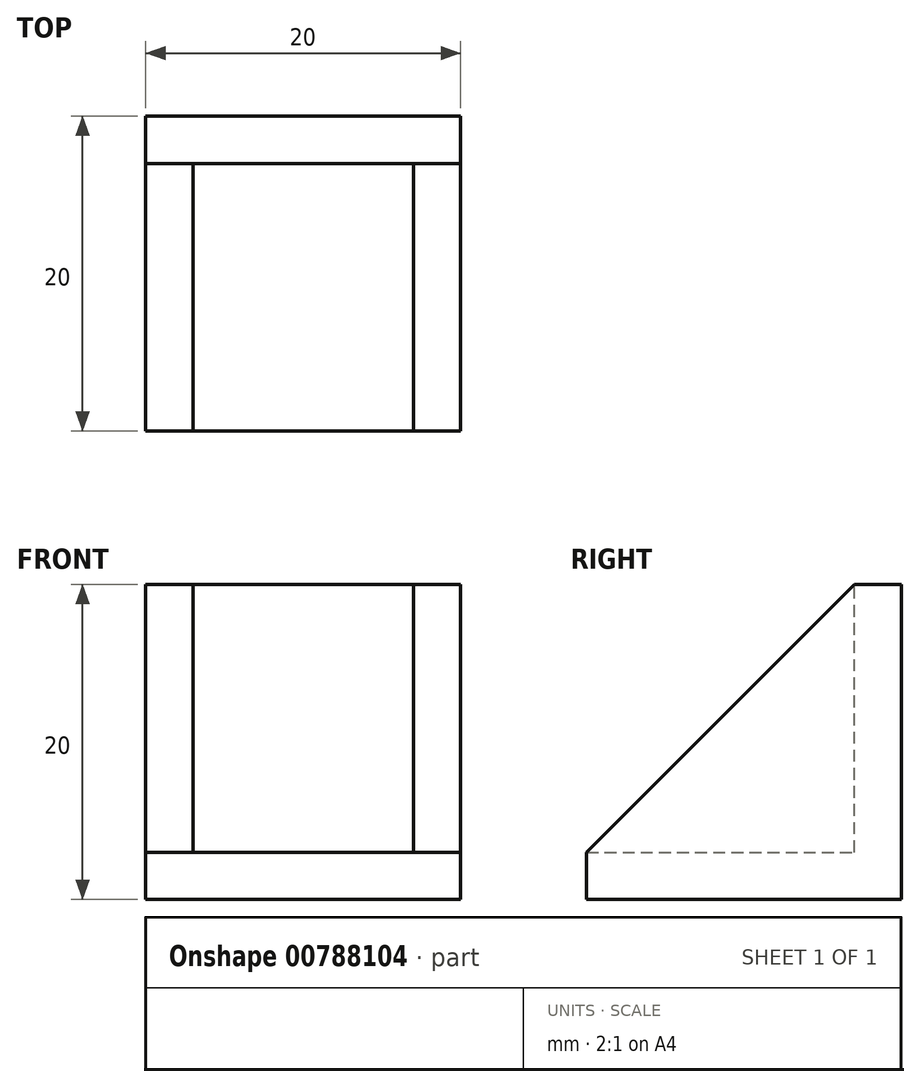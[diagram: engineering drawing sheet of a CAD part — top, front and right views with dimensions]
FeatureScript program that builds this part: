
annotation { "Feature Type Name" : "Feature", "Feature Type Description" : "" }
export const myFeature = defineFeature(function(context is Context, id is Id, definition is map)
    precondition{}
    {
        {
            var Q0;
            Q0=qCreatedBy(makeId("Front.planeOp"),FACE);
            var sketch = newSketch(context, id + "F0", { "sketchPlane" : qUnion([Q0])});
            skLineSegment(sketch, "E0.bottom", {"start": v(0, 0) * mm, "end": v(20, 0) * mm});
            skLineSegment(sketch, "E0.top", {"start": v(0, 20) * mm, "end": v(20, 20) * mm});
            skLineSegment(sketch, "E0.left", {"start": v(0, 0) * mm, "end": v(0, 20) * mm});
            skLineSegment(sketch, "E0.right", {"start": v(20, 0) * mm, "end": v(20, 20) * mm});
            skLineSegment(sketch, "E1", {"start": v(10, 0) * mm, "end": v(10, 8.5) * mm, "construction": true});
            skLineSegment(sketch, "E2", {"start": v(10, 8.5) * mm, "end": v(10, 11.5) * mm, "construction": true});
            skCircle(sketch, "E3", {"center": v(10, 8.5) * mm, "radius": 3 * mm});
            skCircle(sketch, "E4", {"center": v(10, 11.5) * mm, "radius": 3 * mm});
            skLineSegment(sketch, "E5", {"start": v(13, 11.5) * mm, "end": v(13, 8.5) * mm});
            skLineSegment(sketch, "E6", {"start": v(7, 8.5) * mm, "end": v(7, 11.5) * mm});
            skLineSegment(sketch, "E7", {"start": v(20, 0) * mm, "end": v(17, 0) * mm});
            skLineSegment(sketch, "E8", {"start": v(17, 0) * mm, "end": v(17, 20) * mm});
            skLineSegment(sketch, "E9", {"start": v(0, 0) * mm, "end": v(3, 0) * mm});
            skLineSegment(sketch, "E10", {"start": v(3, 0) * mm, "end": v(3, 20) * mm});
            skLineSegment(sketch, "E11", {"start": v(0, 0) * mm, "end": v(0, 3) * mm});
            skLineSegment(sketch, "E12", {"start": v(0, 3) * mm, "end": v(20, 3) * mm});
            skSolve(sketch);
        }
        {
            var Q0;
            {var subQ0=sQuery(id+"F0.wireOp",EDGE,"E0.right");var subQ1=sQuery(id+"F0.wireOp",EDGE,"E0.top");var subQ2=makeQuery(id+"F0.imprint","INTERSECT",VERTEX,{"derivedFrom":[subQ1,subQ0]});Q0=makeQuery(id+"F0.imprint","IMPRINT",FACE,{"disambiguationData":[TD([[makeQuery(id+"F0.imprint","IMPRINT",EDGE,{"disambiguationData":[TD([[subQ2,1.0]])],"derivedFrom":subQ1}),-1.0]])]});}
            var Q1;
            {var subQ0=sQuery(id+"F0.wireOp",EDGE,"E10");var subQ1=sQuery(id+"F0.wireOp",EDGE,"E0.top");var subQ2=makeQuery(id+"F0.imprint","INTERSECT",VERTEX,{"derivedFrom":[subQ1,subQ0]});Q1=makeQuery(id+"F0.imprint","IMPRINT",FACE,{"disambiguationData":[TD([[makeQuery(id+"F0.imprint","IMPRINT",EDGE,{"disambiguationData":[TD([[subQ2,1.0]])],"derivedFrom":subQ1}),-1.0]])]});}
            var Q2;
            {var subQ0=sQuery(id+"F0.wireOp",EDGE,"E10");var subQ1=sQuery(id+"F0.wireOp",EDGE,"E0.bottom");var subQ2=makeQuery(id+"F0.imprint","INTERSECT",VERTEX,{"derivedFrom":[subQ1,subQ0]});Q2=makeQuery(id+"F0.imprint","IMPRINT",FACE,{"disambiguationData":[TD([[makeQuery(id+"F0.imprint","IMPRINT",EDGE,{"disambiguationData":[TD([[subQ2,1.0]])],"derivedFrom":subQ1}),1.0]])]});}
            var Q3;
            {var subQ0=sQuery(id+"F0.wireOp",EDGE,"E10");var subQ1=sQuery(id+"F0.wireOp",EDGE,"E0.bottom");var subQ2=makeQuery(id+"F0.imprint","INTERSECT",VERTEX,{"derivedFrom":[subQ1,subQ0]});Q3=makeQuery(id+"F0.imprint","IMPRINT",FACE,{"disambiguationData":[TD([[makeQuery(id+"F0.imprint","IMPRINT",EDGE,{"disambiguationData":[TD([[subQ2,-1.0]])],"derivedFrom":subQ1}),1.0]])]});}
            var Q4;
            {var subQ0=sQuery(id+"F0.wireOp",EDGE,"E0.right");var subQ1=sQuery(id+"F0.wireOp",EDGE,"E0.bottom");var subQ2=makeQuery(id+"F0.imprint","INTERSECT",VERTEX,{"derivedFrom":[subQ1,subQ0]});Q4=makeQuery(id+"F0.imprint","IMPRINT",FACE,{"disambiguationData":[TD([[makeQuery(id+"F0.imprint","IMPRINT",EDGE,{"disambiguationData":[TD([[subQ2,1.0]])],"derivedFrom":subQ1}),1.0]])]});}
            extrude(context, id + "F1", {"entities" : qUnion([Q0, Q1, Q2, Q3, Q4]), "depth" : 20 * mm, "offsetDistance" : 25 * mm});
        }
        {
            var Q0;
            {var subQ0=sQuery(id+"F0.wireOp",EDGE,"E5");Q0=makeQuery(id+"F0.imprint","IMPRINT",FACE,{"disambiguationData":[TD([[makeQuery(id+"F0.imprint","IMPRINT",EDGE,{"derivedFrom":subQ0}),1.0]])]});}
            var Q1;
            {var subQ0=sQuery(id+"F0.wireOp",EDGE,"E3");var subQ1=makeQuery(id+"F0.imprint","INTERSECT",VERTEX,{"derivedFrom":[subQ0,sQuery(id+"F0.wireOp",EDGE,"E5")]});Q1=makeQuery(id+"F0.imprint","IMPRINT",FACE,{"disambiguationData":[TD([[makeQuery(id+"F0.imprint","IMPRINT",EDGE,{"disambiguationData":[TD([[subQ1,-1.0]])],"derivedFrom":subQ0}),1.0]])]});}
            var Q2;
            {var subQ0=sQuery(id+"F0.wireOp",EDGE,"E4");var subQ1=sQuery(id+"F0.wireOp",EDGE,"E3");var subQ2=makeQuery(id+"F0.imprint","INTERSECT",VERTEX,{"disambiguationData":[OD(0.0)],"derivedFrom":[subQ1,subQ0]});Q2=makeQuery(id+"F0.imprint","IMPRINT",FACE,{"disambiguationData":[TD([[makeQuery(id+"F0.imprint","IMPRINT",EDGE,{"disambiguationData":[TD([[subQ2,-1.0]])],"derivedFrom":subQ1}),1.0]])]});}
            var Q3;
            {var subQ0=sQuery(id+"F0.wireOp",EDGE,"E4");var subQ1=sQuery(id+"F0.wireOp",EDGE,"E3");var subQ2=makeQuery(id+"F0.imprint","INTERSECT",VERTEX,{"disambiguationData":[OD(0.0)],"derivedFrom":[subQ1,subQ0]});Q3=makeQuery(id+"F0.imprint","IMPRINT",FACE,{"disambiguationData":[TD([[makeQuery(id+"F0.imprint","IMPRINT",EDGE,{"disambiguationData":[TD([[subQ2,-1.0]])],"derivedFrom":subQ1}),-1.0]])]});}
            var Q4;
            {var subQ0=sQuery(id+"F0.wireOp",EDGE,"E5");Q4=makeQuery(id+"F0.imprint","IMPRINT",FACE,{"disambiguationData":[TD([[makeQuery(id+"F0.imprint","IMPRINT",EDGE,{"derivedFrom":subQ0}),-1.0]])]});}
            var Q5;
            {var subQ0=sQuery(id+"F0.wireOp",EDGE,"E6");Q5=makeQuery(id+"F0.imprint","IMPRINT",FACE,{"disambiguationData":[TD([[makeQuery(id+"F0.imprint","IMPRINT",EDGE,{"derivedFrom":subQ0}),-1.0]])]});}
            extrude(context, id + "F2", {"entities" : qUnion([Q0, Q1, Q2, Q3, Q4, Q5]), "operationType" : NewBodyOperationType.ADD, "depth" : 3 * mm, "offsetDistance" : 25 * mm});
        }
        {
            var Q0;
            {var subQ0=sQuery(id+"F0.wireOp",EDGE,"E0.top");Q0=makeQuery(id+"F1.opExtrude","CAP_EDGE",EDGE,{"disambiguationData":[OSD([subQ0]),TDD([makeQuery(id+"F0.imprint","IMPRINT",EDGE,{"disambiguationData":[TD([[makeQuery(id+"F0.imprint","INTERSECT",VERTEX,{"derivedFrom":[subQ0,sQuery(id+"F0.wireOp",EDGE,"E10")]}),1.0]])],"derivedFrom":subQ0})])],"isStart":false});}
            var Q1;
            {var subQ0=sQuery(id+"F0.wireOp",EDGE,"E0.top");Q1=makeQuery(id+"F1.opExtrude","CAP_EDGE",EDGE,{"disambiguationData":[OSD([subQ0]),TDD([makeQuery(id+"F0.imprint","IMPRINT",EDGE,{"disambiguationData":[TD([[makeQuery(id+"F0.imprint","INTERSECT",VERTEX,{"derivedFrom":[subQ0,sQuery(id+"F0.wireOp",EDGE,"E0.right")]}),1.0]])],"derivedFrom":subQ0})])],"isStart":false});}
            chamfer(context, id + "F3", {"entities" : qUnion([Q0, Q1]), "width" : 17 * mm, "tangentPropagation" : true});
        }
    });
